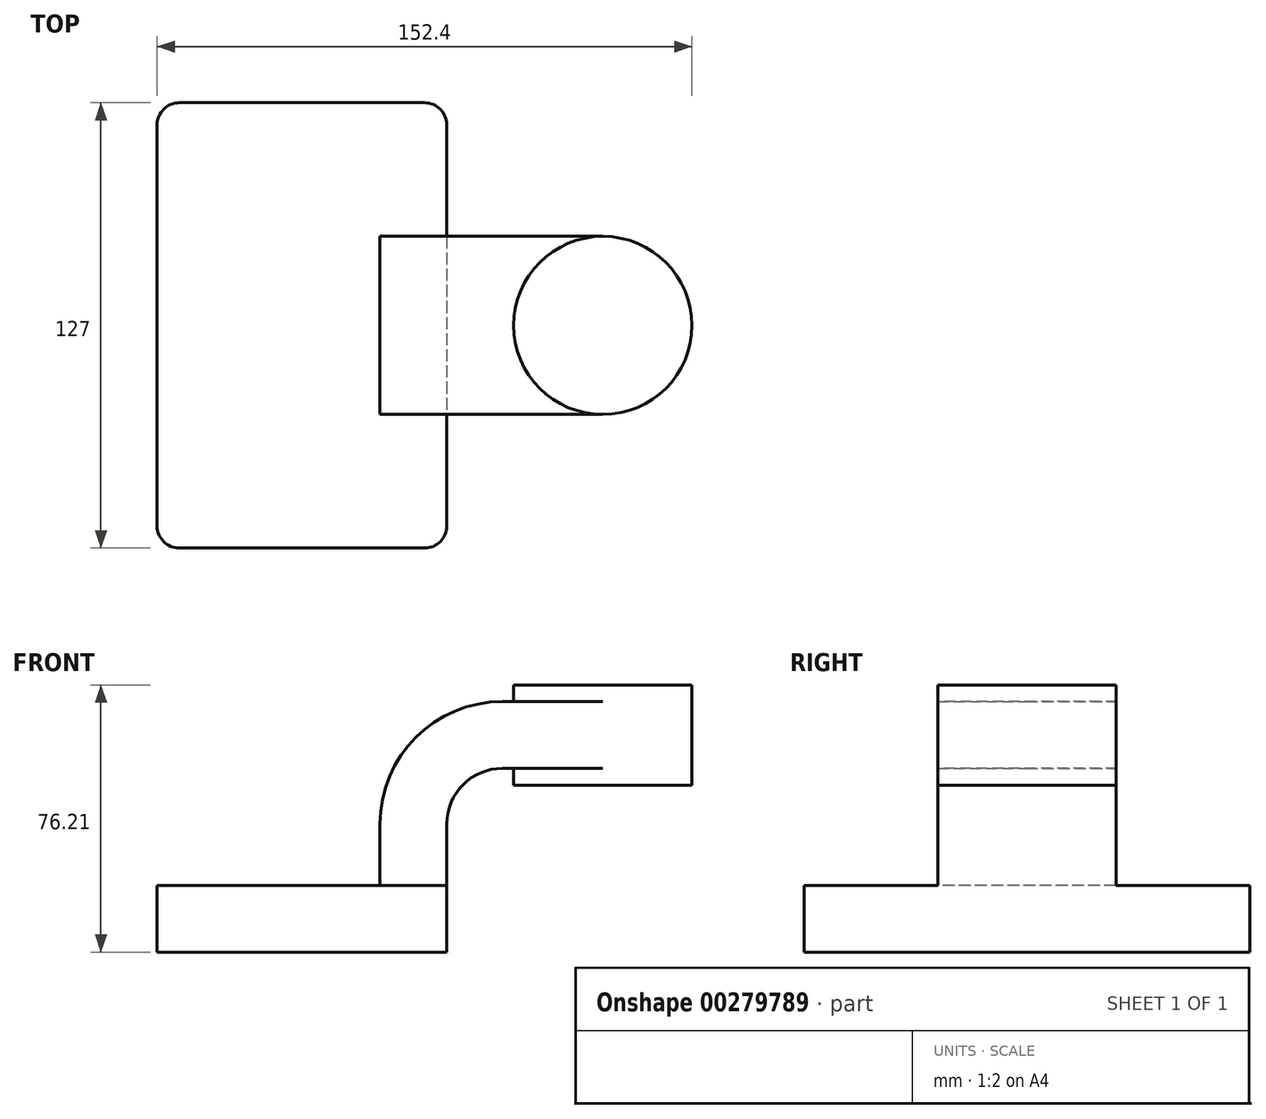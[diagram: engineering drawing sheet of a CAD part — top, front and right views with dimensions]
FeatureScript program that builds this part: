
annotation { "Feature Type Name" : "Feature", "Feature Type Description" : "" }
export const myFeature = defineFeature(function(context is Context, id is Id, definition is map)
    precondition{}
    {
        {
            var Q0;
            Q0=qCreatedBy(makeId("Front.planeOp"),FACE);
            var sketch = newSketch(context, id + "F0", { "sketchPlane" : qUnion([Q0])});
            skLineSegment(sketch, "E0.bottom", {"start": v(41.28, -9.52) * mm, "end": v(-41.28, -9.52) * mm});
            skLineSegment(sketch, "E0.top", {"start": v(41.28, 9.53) * mm, "end": v(-41.28, 9.53) * mm});
            skLineSegment(sketch, "E0.left", {"start": v(41.28, -9.52) * mm, "end": v(41.27, 9.53) * mm});
            skLineSegment(sketch, "E0.right", {"start": v(-41.27, -9.52) * mm, "end": v(-41.28, 9.53) * mm});
            skPoint(sketch, "E0.middle", {"position": v(0, 0) * mm});
            skLineSegment(sketch, "E1", {"start": v(41.28, 9.53) * mm, "end": v(41.28, 27) * mm});
            skArc(sketch, "E2", {"start": v(41.27, 27) * mm, "mid": v(45.92, 38.23) * mm, "end": v(57.15, 42.88) * mm});
            skLineSegment(sketch, "E3", {"start": v(57.15, 42.88) * mm, "end": v(85.72, 42.88) * mm});
            skLineSegment(sketch, "E4.bottom", {"start": v(111.12, 38.1) * mm, "end": v(60.32, 38.1) * mm});
            skLineSegment(sketch, "E4.top", {"start": v(111.12, 66.68) * mm, "end": v(60.32, 66.68) * mm});
            skLineSegment(sketch, "E4.left", {"start": v(111.12, 38.1) * mm, "end": v(111.12, 66.68) * mm});
            skLineSegment(sketch, "E4.right", {"start": v(60.32, 38.1) * mm, "end": v(60.32, 66.68) * mm});
            skPoint(sketch, "E4.middle", {"position": v(85.72, 52.39) * mm});
            skLineSegment(sketch, "E5.0", {"start": v(57.15, 61.93) * mm, "end": v(85.72, 61.93) * mm});
            skArc(sketch, "E5.1", {"start": v(22.22, 27) * mm, "mid": v(32.45, 51.7) * mm, "end": v(57.15, 61.93) * mm});
            skLineSegment(sketch, "E5.2", {"start": v(22.22, 9.53) * mm, "end": v(22.22, 27) * mm});
            skLineSegment(sketch, "E6", {"start": v(85.72, 38.1) * mm, "end": v(85.72, 66.68) * mm});
            skFitSpline(sketch, "E7", {"points": [v(-41.28, 9.52) * mm, v(57.15, 61.93) * mm], "startDerivative": vector(0, 156.37) * mm, "endDerivative": vector(105.41, 0) * mm});
            skSolve(sketch);
        }
        {
            var Q0;
            Q0=makeQuery(id+"F0.imprint","IMPRINT",FACE,{"disambiguationData":[TD([[makeQuery(id+"F0.imprint","IMPRINT",EDGE,{"derivedFrom":sQuery(id+"F0.wireOp",EDGE,"E0.bottom")}),-1.0]])]});
            extrude(context, id + "F1", {"entities" : qUnion([Q0]), "endBound" : BoundingType.SYMMETRIC, "oppositeDirection" : true, "depth" : 127 * mm});
        }
        {
            var Q0;
            {var subQ7=sQuery(id+"F0.wireOp",EDGE,"E1");Q0=makeQuery(id+"F0.imprint","IMPRINT",FACE,{"disambiguationData":[TD([[makeQuery(id+"F0.imprint","IMPRINT",EDGE,{"derivedFrom":subQ7}),1.0]])]});}
            var Q1;
            {var subQ0=sQuery(id+"F0.wireOp",EDGE,"E6");var subQ1=sQuery(id+"F0.wireOp",EDGE,"E3");var subQ2=makeQuery(id+"F0.imprint","INTERSECT",VERTEX,{"derivedFrom":[subQ1,subQ0]});Q1=makeQuery(id+"F0.imprint","IMPRINT",FACE,{"disambiguationData":[TD([[makeQuery(id+"F0.imprint","IMPRINT",EDGE,{"disambiguationData":[TD([[subQ2,1.0]])],"derivedFrom":subQ1}),1.0]])]});}
            extrude(context, id + "F2", {"entities" : qUnion([Q0, Q1]), "operationType" : NewBodyOperationType.ADD, "endBound" : BoundingType.SYMMETRIC, "oppositeDirection" : true, "depth" : 50.8 * mm});
        }
        {
            var Q0;
            Q0=makeQuery(id+"F0.imprint","IMPRINT",FACE,{"disambiguationData":[TD([[makeQuery(id+"F0.imprint","IMPRINT",EDGE,{"derivedFrom":sQuery(id+"F0.wireOp",EDGE,"E5.1")}),1.0]])]});
            extrude(context, id + "F3", {"entities" : qUnion([Q0]), "operationType" : NewBodyOperationType.ADD, "endBound" : BoundingType.SYMMETRIC, "depth" : 15.88 * mm});
        }
        {
            var Q0;
            {var subQ4=sQuery(id+"F0.wireOp",EDGE,"E4.left");Q0=makeQuery(id+"F0.imprint","IMPRINT",FACE,{"disambiguationData":[TD([[makeQuery(id+"F0.imprint","IMPRINT",EDGE,{"derivedFrom":subQ4}),1.0]])]});}
            var Q1;
            Q1=sQuery(id+"F0.wireOp",EDGE,"E6");
            revolve(context, id + "F4", {"operationType" : NewBodyOperationType.ADD, "entities" : qUnion([Q0]), "axis" : qUnion([Q1]), "revolveType" : RevolveType.FULL});
        }
        {
            var Q0;
            Q0=makeQuery(id+"F1.opExtrude","CAP_EDGE",EDGE,{"disambiguationData":[OSD([sQuery(id+"F0.wireOp",EDGE,"E0.right")])],"isStart":true});
            var Q1;
            Q1=makeQuery(id+"F1.opExtrude","CAP_EDGE",EDGE,{"disambiguationData":[OSD([sQuery(id+"F0.wireOp",EDGE,"E0.left")])],"isStart":true});
            var Q2;
            Q2=makeQuery(id+"F1.opExtrude","CAP_EDGE",EDGE,{"disambiguationData":[OSD([sQuery(id+"F0.wireOp",EDGE,"E0.right")])],"isStart":false});
            var Q3;
            Q3=makeQuery(id+"F1.opExtrude","CAP_EDGE",EDGE,{"disambiguationData":[OSD([sQuery(id+"F0.wireOp",EDGE,"E0.left")])],"isStart":false});
            fillet(context, id + "F5", {"entities" : qUnion([Q0, Q1, Q2, Q3]), "radius" : 6.35 * mm, "tangentPropagation" : true, "allowEdgeOverflow" : false});
        }
    });
